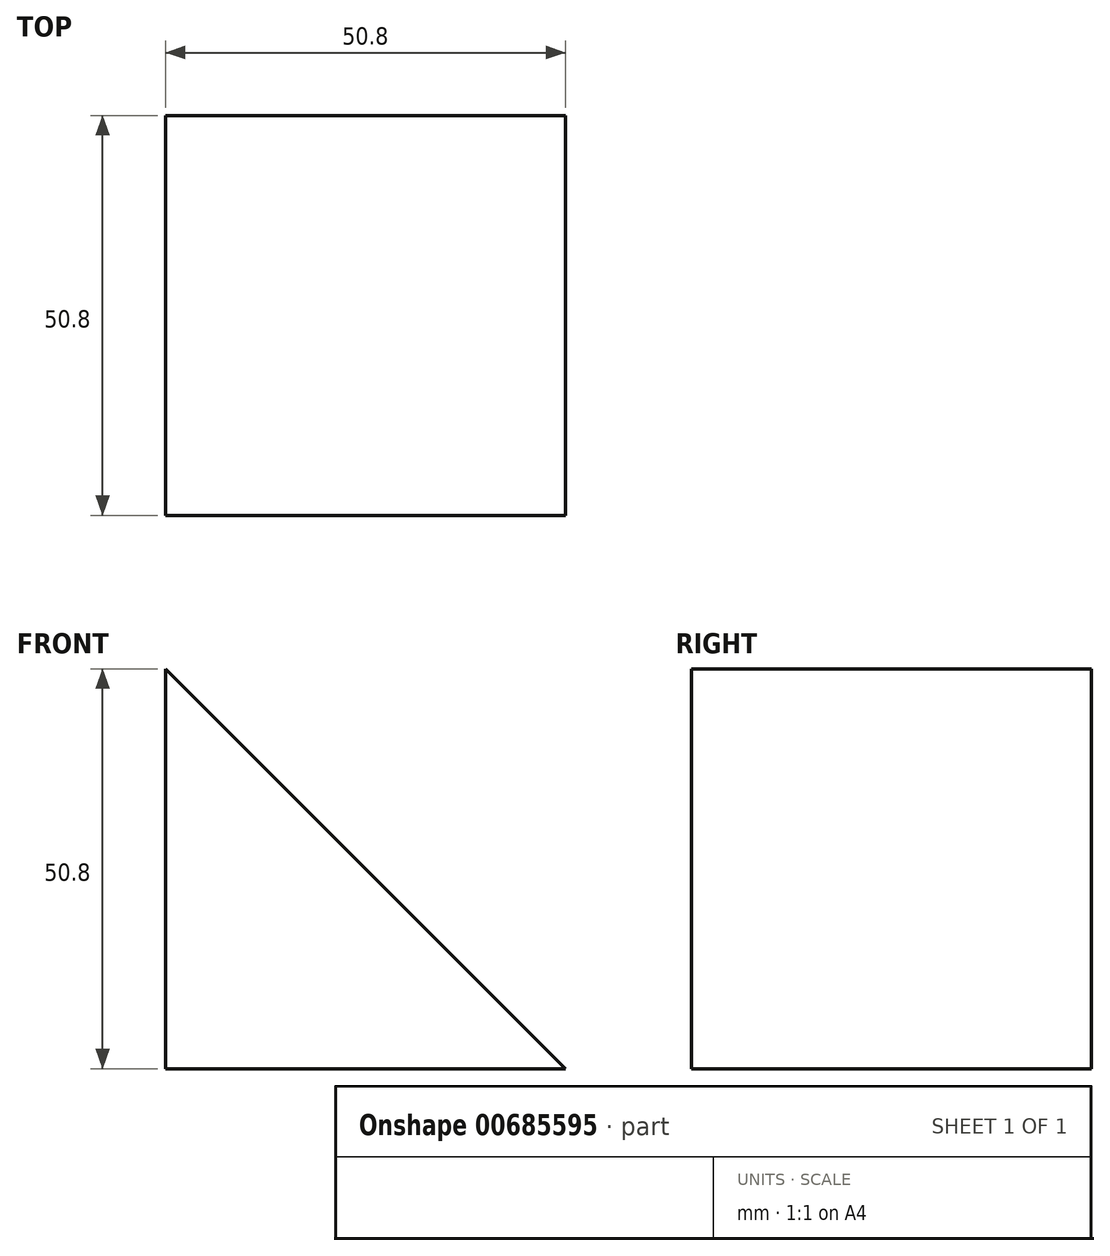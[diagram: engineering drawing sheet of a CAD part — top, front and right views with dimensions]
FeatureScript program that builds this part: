
annotation { "Feature Type Name" : "Feature", "Feature Type Description" : "" }
export const myFeature = defineFeature(function(context is Context, id is Id, definition is map)
    precondition{}
    {
        {
            var Q0;
            Q0=qCreatedBy(makeId("Front.planeOp"),FACE);
            var sketch = newSketch(context, id + "F0", { "sketchPlane" : qUnion([Q0])});
            skLineSegment(sketch, "E0", {"start": v(0, 0) * mm, "end": v(50.8, 0) * mm});
            skLineSegment(sketch, "E1", {"start": v(50.8, 0) * mm, "end": v(0, 0) * mm});
            skLineSegment(sketch, "E2", {"start": v(0, 0) * mm, "end": v(0, 50.8) * mm});
            skLineSegment(sketch, "E3", {"start": v(0, 50.8) * mm, "end": v(50.8, 0) * mm});
            skSolve(sketch);
        }
        {
            var Q0;
            Q0 = qSketchRegion(id + "F0", true);
            extrude(context, id + "F1", {"entities" : qUnion([Q0]), "depth" : 50.8 * mm, "offsetDistance" : 25.4 * mm});
        }
    });
